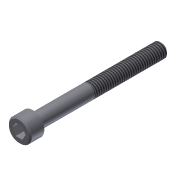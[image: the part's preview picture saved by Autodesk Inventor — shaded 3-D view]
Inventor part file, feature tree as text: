
AUTODESK INVENTOR PART (.ipt)
format: ipt  version: 2013 (Build 170138000, 138)  size: 100,864 bytes
history: native  units: in
note: dims shown in document units (in); Inventor stores cm internally (conversion verified against a paired STEP export)
features: extrude x3, sketch x3, chamfer x2, thread x1
ambient origin geometry x8: Origin, YZ Plane, XZ Plane, XY Plane, X Axis, Y Axis, Z Axis, Center Point
bodies: Solid1 (feature_tree)
feature tree (9):
  extrude  "Extrusion1"  Depth=0.19in TaperAngle=0.0deg
  extrude  "Extrusion2"  Depth=1.75in TaperAngle=0.0deg
  extrude  "Extrusion3"  Depth=0.125in TaperAngle=0.0deg
  thread  "Thread1"  [1 undecoded]
  chamfer  "Chamfer1"  Distance=0.02in Angle=45.0deg
  chamfer  "Chamfer2"  Distance=0.02in Angle=45.0deg
  sketch  "Sketch1"  dims[d0=0.312in d1=0.19in d2=0.0in]
  sketch  "Sketch2"  dims[d3=0.19in d4=1.75in d5=0.0in]
  sketch  "Sketch3"  dims[d6=0.1562in d7=0.125in d8=0.0in d9=1.0in d10=0.0in d11=0.02in d12=0.125in d13=45.0deg d14=0.02in d15=0.125in d16=45.0deg]
note: 1 required parameter value undecoded (feature->parameter linkage not recoverable at this tier; creation-order binding heuristic only, values carry confidence <= 0.55)
